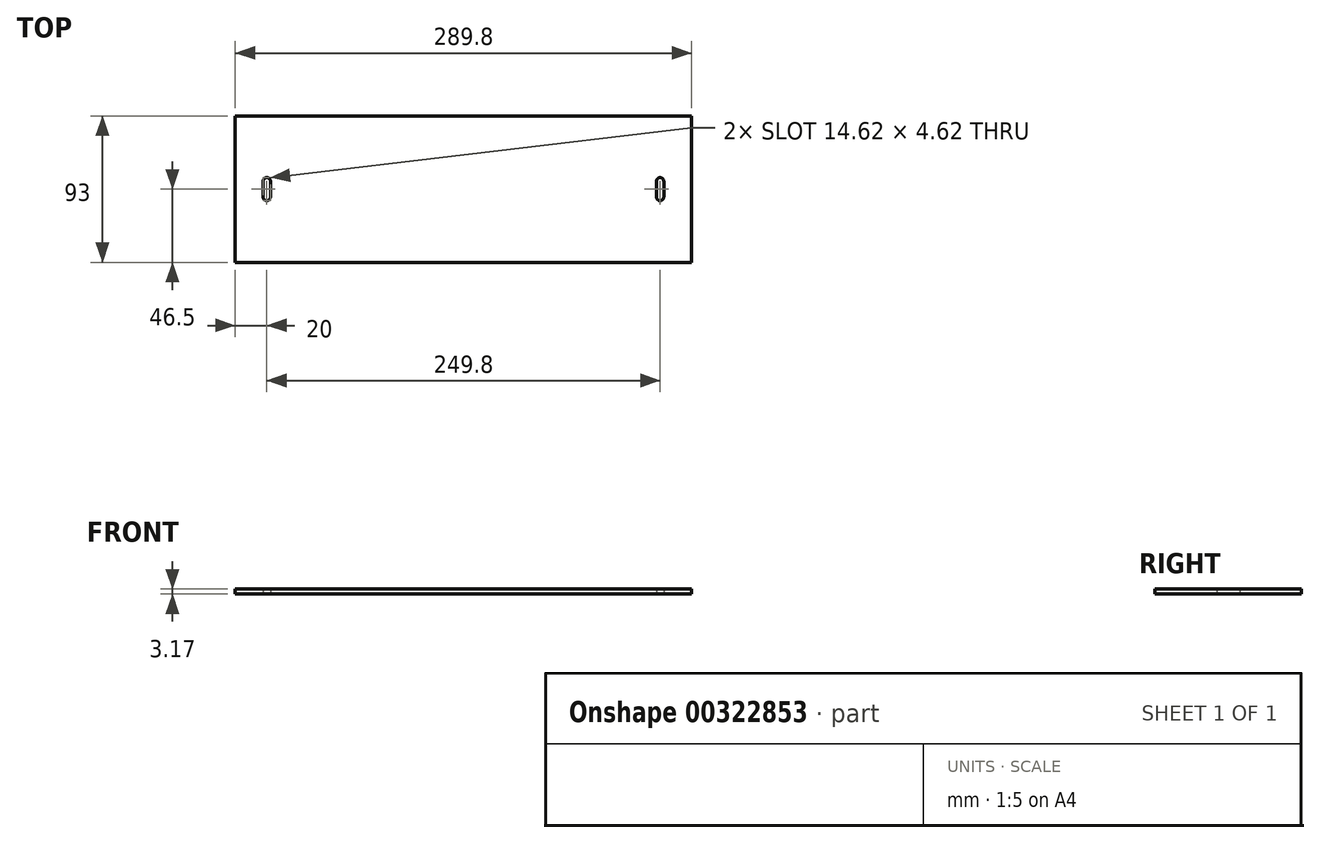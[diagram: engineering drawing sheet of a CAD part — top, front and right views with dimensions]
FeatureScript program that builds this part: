
annotation { "Feature Type Name" : "Feature", "Feature Type Description" : "" }
export const myFeature = defineFeature(function(context is Context, id is Id, definition is map)
    precondition{}
    {
        {
            var Q0;
            Q0=qCreatedBy(makeId("Top.planeOp"),FACE);
            var sketch = newSketch(context, id + "F0", { "sketchPlane" : qUnion([Q0])});
            skLineSegment(sketch, "E0.bottom", {"start": v(144.9, -46.5) * mm, "end": v(-144.9, -46.5) * mm});
            skLineSegment(sketch, "E0.top", {"start": v(144.9, 46.5) * mm, "end": v(-144.9, 46.5) * mm});
            skLineSegment(sketch, "E0.left", {"start": v(144.9, -46.5) * mm, "end": v(144.9, 46.5) * mm});
            skLineSegment(sketch, "E0.right", {"start": v(-144.9, -46.5) * mm, "end": v(-144.9, 46.5) * mm});
            skPoint(sketch, "E0.middle", {"position": v(0, 0) * mm});
            skLineSegment(sketch, "E1", {"start": v(-144.9, 0) * mm, "end": v(-124.9, 0) * mm});
            skPoint(sketch, "E1.endSnap0", {"position": v(-144.9, 0) * mm});
            skLineSegment(sketch, "E2", {"start": v(144.9, 0) * mm, "end": v(124.9, 0) * mm});
            skLineSegment(sketch, "E3.bottom", {"start": v(127.21, -5) * mm, "end": v(122.59, -5) * mm});
            skLineSegment(sketch, "E3.top", {"start": v(127.21, 5) * mm, "end": v(122.59, 5) * mm});
            skLineSegment(sketch, "E3.left", {"start": v(127.21, -5) * mm, "end": v(127.21, 5) * mm});
            skLineSegment(sketch, "E3.right", {"start": v(122.59, -5) * mm, "end": v(122.59, 5) * mm});
            skPoint(sketch, "E3.middle", {"position": v(124.9, 0) * mm});
            skLineSegment(sketch, "E4.bottom", {"start": v(-122.59, 5) * mm, "end": v(-127.21, 5) * mm});
            skLineSegment(sketch, "E4.top", {"start": v(-122.59, -5) * mm, "end": v(-127.21, -5) * mm});
            skLineSegment(sketch, "E4.left", {"start": v(-122.59, 5) * mm, "end": v(-122.59, -5) * mm});
            skLineSegment(sketch, "E4.right", {"start": v(-127.21, 5) * mm, "end": v(-127.21, -5) * mm});
            skPoint(sketch, "E4.middle", {"position": v(-124.9, 0) * mm});
            skCircle(sketch, "E5", {"center": v(-124.9, 5) * mm, "radius": 2.31 * mm});
            skCircle(sketch, "E6", {"center": v(-124.9, -5) * mm, "radius": 2.31 * mm});
            skCircle(sketch, "E7", {"center": v(124.9, 5) * mm, "radius": 2.31 * mm});
            skCircle(sketch, "E8", {"center": v(124.9, -5) * mm, "radius": 2.31 * mm});
            skSolve(sketch);
        }
        {
            var Q0;
            Q0 = qSketchRegion(id + "F0", true);
            extrude(context, id + "F1", {"entities" : qUnion([Q0]), "depth" : 3.17 * mm});
        }
    });
